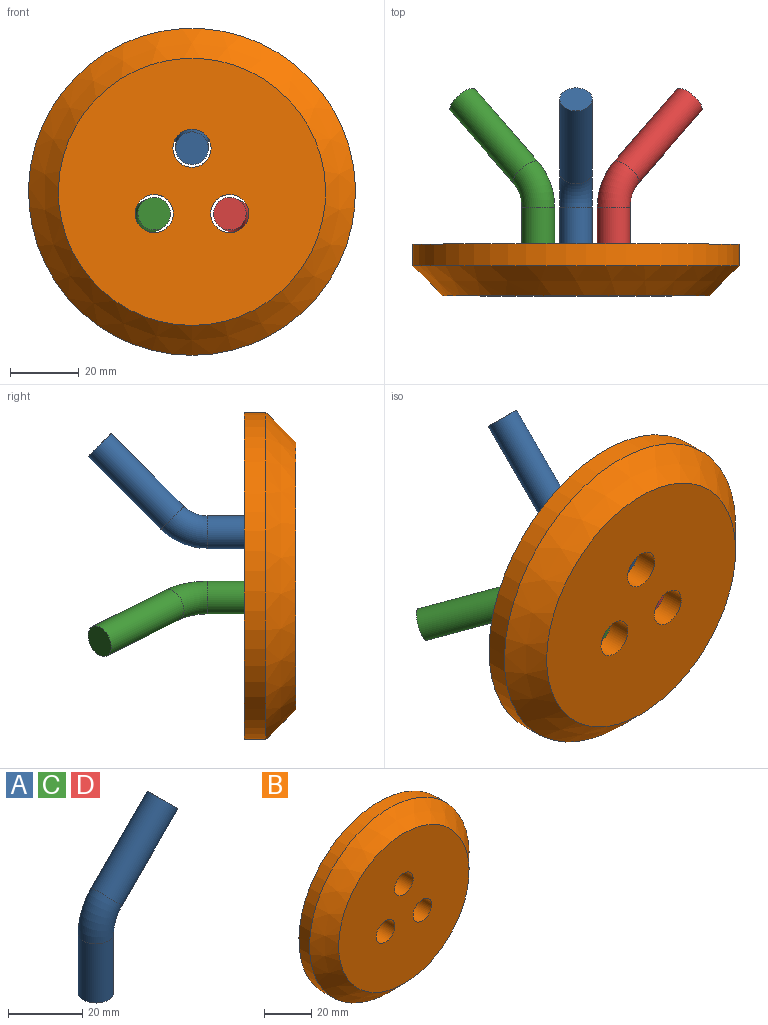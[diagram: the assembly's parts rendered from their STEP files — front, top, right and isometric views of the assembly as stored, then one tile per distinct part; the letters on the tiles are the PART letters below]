
ASSEMBLY  parts=4 mates=1
PART A: 5 faces, bbox 35.1x9.5x54.2 mm
  f0: plane 9.53x9.53mm, normal (0,0,-1), area 71.3mm2, adj f2
  f1: plane 9.53x6.74mm, normal (0.71,0,0.71), area 71.3mm2, adj f4
  f2: cylinder r=4.76mm len=19.48mm, axis (0,0,1), area 583mm2, adj f0,f3
  f3: torus R=14.29mm, axis (0,1,0), area 335.8mm2, adj f2,f4
  f4: cylinder r=4.76mm len=27.95mm, axis (0.71,0,0.71), area 897.8mm2, adj f1,f3
PART B: 7 faces, bbox 95.3x15.1x95.3 mm
  f0: plane 95.25x95.25mm, normal (0,1,0), area 6834.6mm2, adj f1,f4,f5,f6
  f1: cylinder r=47.62mm len=95.25mm, axis (0,-1,0), area 1900.2mm2, adj f0,f2
  f2: cone r=47.62mm half-angle=45deg, axis (0,1,0), area 3347mm2, adj f1,f3
  f3: plane 77.84x77.84mm, normal (0,-1,0), area 4467.9mm2, adj f2,f4,f5,f6
  f4: cylinder r=5.56mm len=15.05mm, axis (0,1,0), area 525.6mm2, adj f0,f3
  f5: cylinder r=5.56mm len=15.05mm, axis (0,1,0), area 525.6mm2, adj f0,f3
  f6: cylinder r=5.56mm len=15.05mm, axis (0,1,0), area 525.6mm2, adj f0,f3
PART C: same geometry as A
PART D: same geometry as A
PLACE A rot(axis=(-0.58,-0.58,-0.58),120deg) t=(-3.85,-2.03,14.76)mm
PLACE B t=(-3.85,6.68,2.06)mm fixed
PLACE C rot(axis=(-0.19,0.69,0.69),158.9deg) t=(-14.85,-2.03,-4.29)mm
PLACE D rot(axis=(-0.94,0.25,0.25),93.8deg) t=(7.14,-2.03,-4.29)mm
MATE fastened A.f2 <-> B.f4  axis (0,-1,0) through (-3.85,-2.03,14.76)mm
